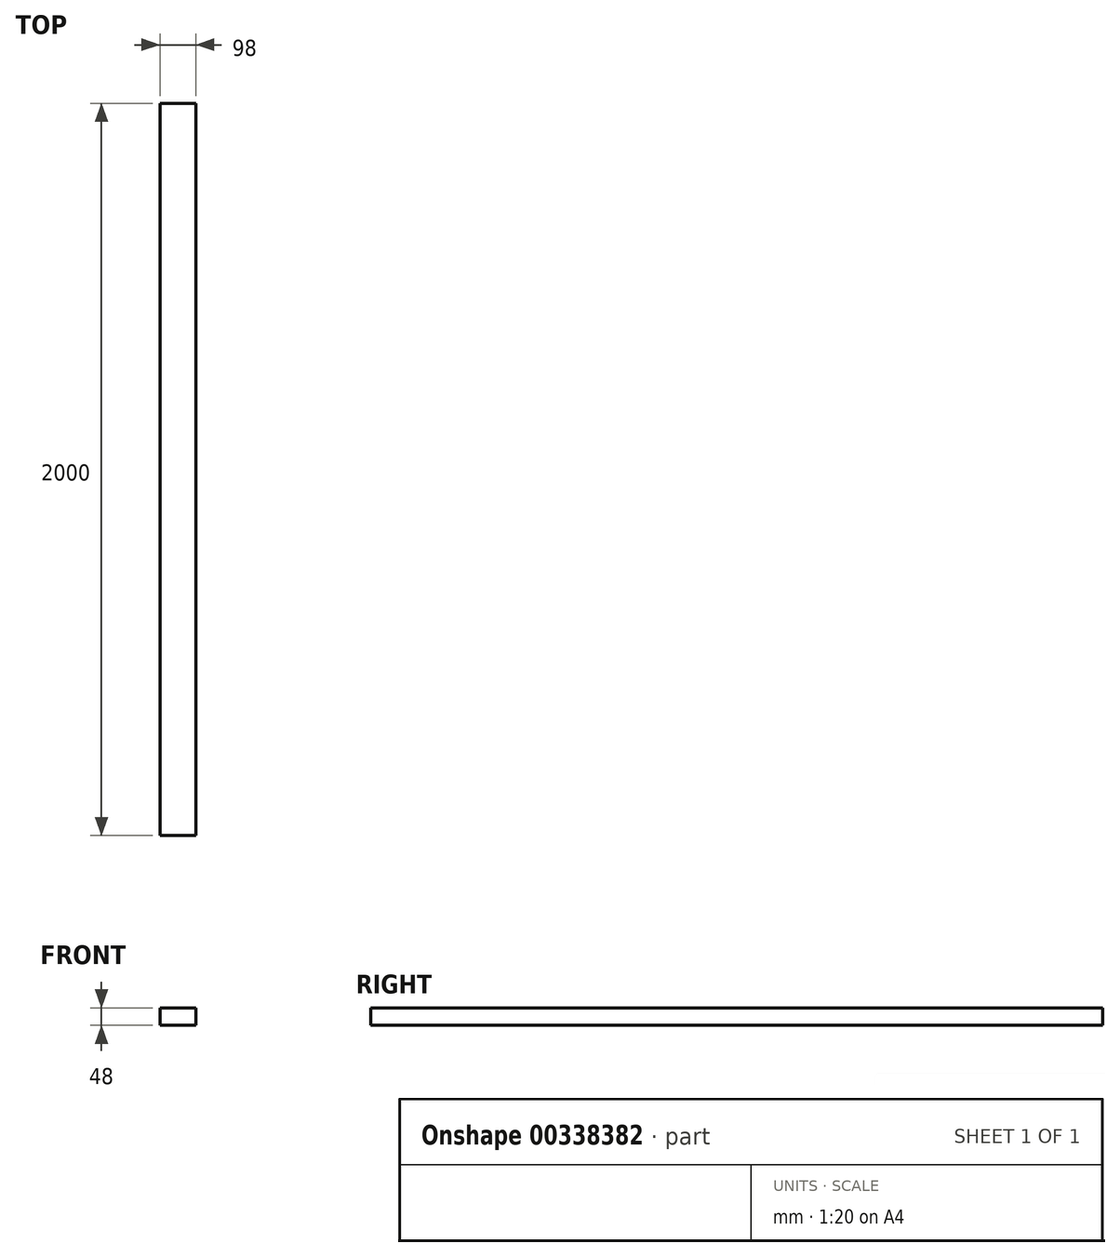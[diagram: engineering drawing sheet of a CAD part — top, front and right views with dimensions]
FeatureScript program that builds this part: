
annotation { "Feature Type Name" : "Feature", "Feature Type Description" : "" }
export const myFeature = defineFeature(function(context is Context, id is Id, definition is map)
    precondition{}
    {
        {
            var Q0;
            Q0=qCreatedBy(makeId("Front.planeOp"),FACE);
            var sketch = newSketch(context, id + "F0", { "sketchPlane" : qUnion([Q0])});
            skLineSegment(sketch, "E0.bottom", {"start": v(-49, -24) * mm, "end": v(49, -24) * mm});
            skLineSegment(sketch, "E0.top", {"start": v(-49, 24) * mm, "end": v(49, 24) * mm});
            skLineSegment(sketch, "E0.left", {"start": v(-49, -24) * mm, "end": v(-49, 24) * mm});
            skLineSegment(sketch, "E0.right", {"start": v(49, -24) * mm, "end": v(49, 24) * mm});
            skPoint(sketch, "E0.middle", {"position": v(0, 0) * mm});
            skSolve(sketch);
        }
        {
            var Q0;
            Q0=makeQuery(id+"F0.imprint","IMPRINT",FACE,{"disambiguationData":[TD([[makeQuery(id+"F0.imprint","IMPRINT",EDGE,{"derivedFrom":sQuery(id+"F0.wireOp",EDGE,"E0.bottom")}),1.0]])]});
            extrude(context, id + "F1", {"entities" : qUnion([Q0]), "depth" : 2000 * mm});
        }
    });
